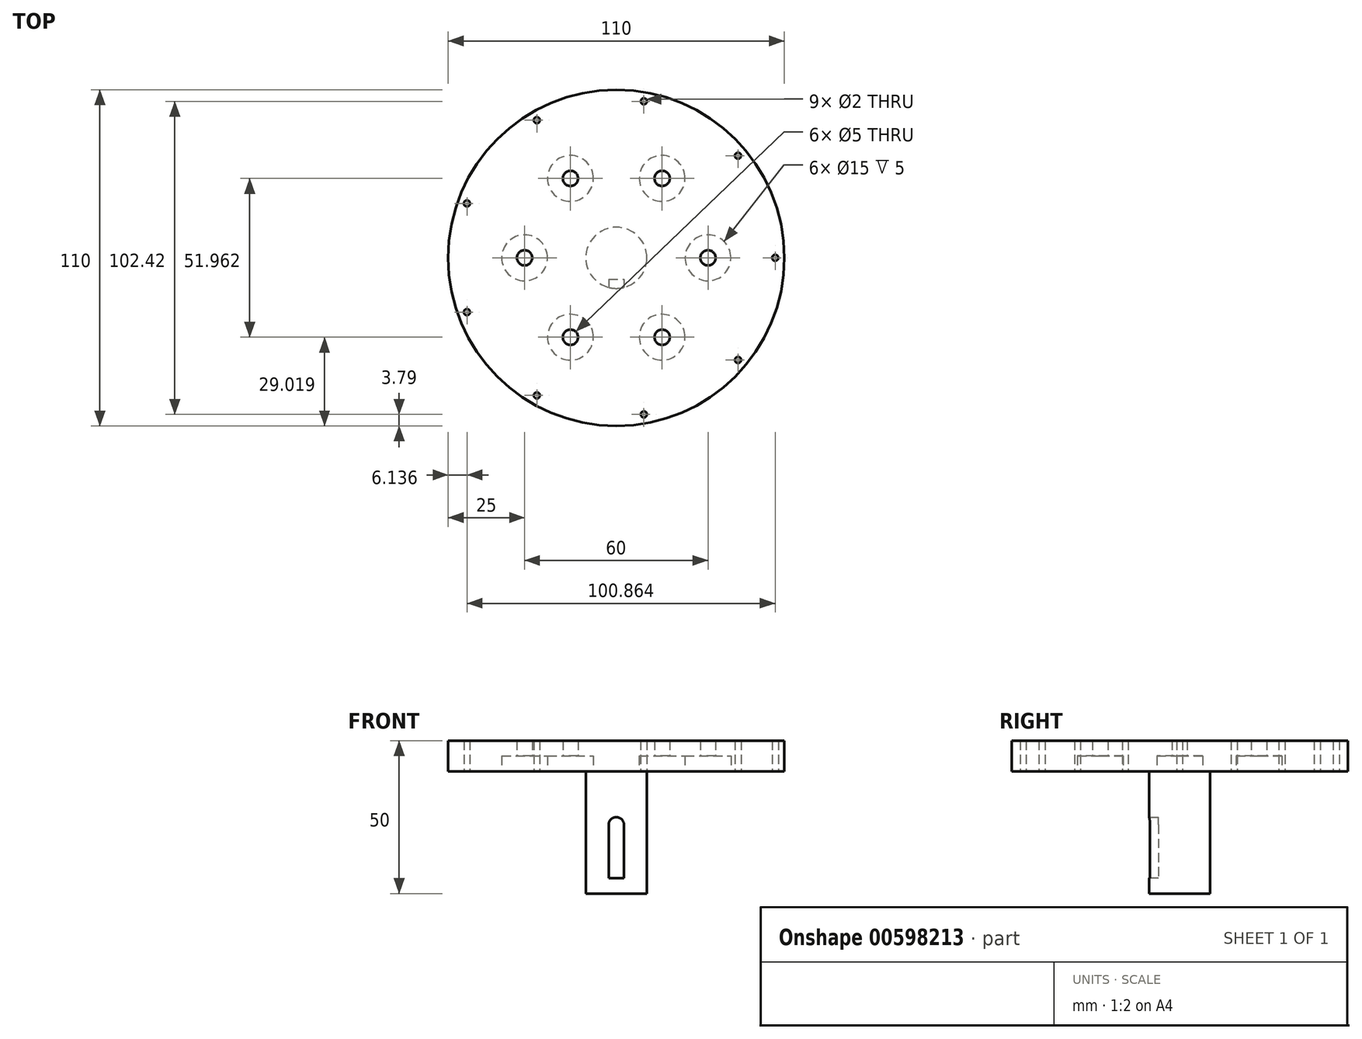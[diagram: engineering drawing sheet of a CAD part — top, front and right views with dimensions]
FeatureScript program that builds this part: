
annotation { "Feature Type Name" : "Feature", "Feature Type Description" : "" }
export const myFeature = defineFeature(function(context is Context, id is Id, definition is map)
    precondition{}
    {
        {
            var Q0;
            Q0=qCreatedBy(makeId("Top.planeOp"),FACE);
            var sketch = newSketch(context, id + "F0", { "sketchPlane" : qUnion([Q0])});
            skCircle(sketch, "E0", {"center": v(0, 0) * mm, "radius": 55 * mm});
            skCircle(sketch, "E1", {"center": v(30, 0) * mm, "radius": 2.5 * mm});
            skCircle(sketch, "E2.1.0", {"center": v(15, 25.98) * mm, "radius": 2.5 * mm});
            skCircle(sketch, "E2.2.0", {"center": v(-15, 25.98) * mm, "radius": 2.5 * mm});
            skCircle(sketch, "E2.3.0", {"center": v(-30, 0) * mm, "radius": 2.5 * mm});
            skCircle(sketch, "E2.4.0", {"center": v(-15, -25.98) * mm, "radius": 2.5 * mm});
            skCircle(sketch, "E2.5.0", {"center": v(15, -25.98) * mm, "radius": 2.5 * mm});
            skCircle(sketch, "E3", {"center": v(0, 0) * mm, "radius": 10 * mm});
            skCircle(sketch, "E4", {"center": v(52, 0) * mm, "radius": 1 * mm});
            skCircle(sketch, "E5.1.0", {"center": v(39.83, 33.42) * mm, "radius": 1 * mm});
            skCircle(sketch, "E5.2.0", {"center": v(9.03, 51.21) * mm, "radius": 1 * mm});
            skCircle(sketch, "E5.3.0", {"center": v(-26, 45.03) * mm, "radius": 1 * mm});
            skCircle(sketch, "E5.4.0", {"center": v(-48.86, 17.79) * mm, "radius": 1 * mm});
            skCircle(sketch, "E5.5.0", {"center": v(-48.86, -17.79) * mm, "radius": 1 * mm});
            skCircle(sketch, "E5.6.0", {"center": v(-26, -45.03) * mm, "radius": 1 * mm});
            skCircle(sketch, "E5.7.0", {"center": v(9.03, -51.21) * mm, "radius": 1 * mm});
            skCircle(sketch, "E5.8.0", {"center": v(39.83, -33.42) * mm, "radius": 1 * mm});
            skSolve(sketch);
        }
        {
            var Q0;
            Q0 = qSketchRegion(id + "F0", true);
            var Q1;
            Q1=makeQuery(id+"F0.imprint","IMPRINT",FACE,{"disambiguationData":[TD([[makeQuery(id+"F0.imprint","IMPRINT",EDGE,{"derivedFrom":sQuery(id+"F0.wireOp",EDGE,"E3")}),1.0]])]});
            extrude(context, id + "F1", {"entities" : qUnion([Q0, Q1]), "depth" : 50 * mm, "offsetDistance" : 25 * mm});
        }
        {
            var Q0;
            Q0 = qSketchRegion(id + "F0", true);
            var Q1;
            Q1=makeQuery(id+"F1.opExtrude","CAP_FACE",FACE,{"disambiguationData":[OSD([sQuery(id+"F0.wireOp",EDGE,"E0"),sQuery(id+"F0.wireOp",EDGE,"E1"),sQuery(id+"F0.wireOp",EDGE,"E2.1.0"),sQuery(id+"F0.wireOp",EDGE,"E2.2.0"),sQuery(id+"F0.wireOp",EDGE,"E2.3.0"),sQuery(id+"F0.wireOp",EDGE,"E2.4.0"),sQuery(id+"F0.wireOp",EDGE,"E2.5.0"),sQuery(id+"F0.wireOp",EDGE,"4EDKuiju-nCJj-Tv50-iLBq-kj0HRudPTFIA"),sQuery(id+"F0.wireOp",EDGE,"37c3f761-c143-4761-86c4-4c0452dd75e1.1.0"),sQuery(id+"F0.wireOp",EDGE,"37c3f761-c143-4761-86c4-4c0452dd75e1.2.0"),sQuery(id+"F0.wireOp",EDGE,"37c3f761-c143-4761-86c4-4c0452dd75e1.3.0"),sQuery(id+"F0.wireOp",EDGE,"37c3f761-c143-4761-86c4-4c0452dd75e1.4.0"),sQuery(id+"F0.wireOp",EDGE,"37c3f761-c143-4761-86c4-4c0452dd75e1.5.0"),sQuery(id+"F0.wireOp",EDGE,"37c3f761-c143-4761-86c4-4c0452dd75e1.6.0")])],"isStart":false});
            extrude(context, id + "F2", {"entities" : qUnion([Q0, Q1]), "operationType" : NewBodyOperationType.REMOVE, "depth" : 40 * mm, "offsetDistance" : 25 * mm});
        }
        {
            var Q0;
            Q0=makeQuery(id+"F2.boolean.opBoolean","COPY",FACE,{"derivedFrom":makeQuery(id+"F2.opExtrude","CAP_FACE",FACE,{"disambiguationData":[OSD([sQuery(id+"F0.wireOp",EDGE,"E0"),sQuery(id+"F0.wireOp",EDGE,"E1"),sQuery(id+"F0.wireOp",EDGE,"E2.1.0"),sQuery(id+"F0.wireOp",EDGE,"E2.2.0"),sQuery(id+"F0.wireOp",EDGE,"E2.3.0"),sQuery(id+"F0.wireOp",EDGE,"E2.4.0"),sQuery(id+"F0.wireOp",EDGE,"E2.5.0"),sQuery(id+"F0.wireOp",EDGE,"E3"),sQuery(id+"F0.wireOp",EDGE,"4EDKuiju-nCJj-Tv50-iLBq-kj0HRudPTFIA"),sQuery(id+"F0.wireOp",EDGE,"37c3f761-c143-4761-86c4-4c0452dd75e1.1.0"),sQuery(id+"F0.wireOp",EDGE,"37c3f761-c143-4761-86c4-4c0452dd75e1.2.0"),sQuery(id+"F0.wireOp",EDGE,"37c3f761-c143-4761-86c4-4c0452dd75e1.3.0"),sQuery(id+"F0.wireOp",EDGE,"37c3f761-c143-4761-86c4-4c0452dd75e1.4.0"),sQuery(id+"F0.wireOp",EDGE,"37c3f761-c143-4761-86c4-4c0452dd75e1.5.0"),sQuery(id+"F0.wireOp",EDGE,"37c3f761-c143-4761-86c4-4c0452dd75e1.6.0")])],"isStart":false})});
            var sketch = newSketch(context, id + "F3", { "sketchPlane" : qUnion([Q0])});
            skCircle(sketch, "E6", {"center": v(15, -25.98) * mm, "radius": 7.5 * mm});
            skCircle(sketch, "E7.1.0", {"center": v(30, 0) * mm, "radius": 7.5 * mm});
            skCircle(sketch, "E7.2.0", {"center": v(15, 25.98) * mm, "radius": 7.5 * mm});
            skCircle(sketch, "E7.3.0", {"center": v(-15, 25.98) * mm, "radius": 7.5 * mm});
            skCircle(sketch, "E7.4.0", {"center": v(-30, 0) * mm, "radius": 7.5 * mm});
            skCircle(sketch, "E7.5.0", {"center": v(-15, -25.98) * mm, "radius": 7.5 * mm});
            skPoint(sketch, "E7.center", {"position": v(0, 0) * mm});
            skSolve(sketch);
        }
        {
            var Q0;
            Q0=makeQuery(id+"F3.imprint","IMPRINT",FACE,{"disambiguationData":[TD([[makeQuery(id+"F3.imprint","IMPRINT",EDGE,{"derivedFrom":sQuery(id+"F3.wireOp",EDGE,"E6")}),1.0]])]});
            var Q1;
            Q1=makeQuery(id+"F3.imprint","IMPRINT",FACE,{"disambiguationData":[TD([[makeQuery(id+"F3.imprint","IMPRINT",EDGE,{"derivedFrom":sQuery(id+"F3.wireOp",EDGE,"E7.1.0")}),1.0]])]});
            var Q2;
            Q2=makeQuery(id+"F3.imprint","IMPRINT",FACE,{"disambiguationData":[TD([[makeQuery(id+"F3.imprint","IMPRINT",EDGE,{"derivedFrom":sQuery(id+"F3.wireOp",EDGE,"E7.5.0")}),1.0]])]});
            var Q3;
            Q3=makeQuery(id+"F3.imprint","IMPRINT",FACE,{"disambiguationData":[TD([[makeQuery(id+"F3.imprint","IMPRINT",EDGE,{"derivedFrom":sQuery(id+"F3.wireOp",EDGE,"E7.2.0")}),1.0]])]});
            var Q4;
            Q4=makeQuery(id+"F3.imprint","IMPRINT",FACE,{"disambiguationData":[TD([[makeQuery(id+"F3.imprint","IMPRINT",EDGE,{"derivedFrom":sQuery(id+"F3.wireOp",EDGE,"E7.3.0")}),1.0]])]});
            var Q5;
            Q5=makeQuery(id+"F3.imprint","IMPRINT",FACE,{"disambiguationData":[TD([[makeQuery(id+"F3.imprint","IMPRINT",EDGE,{"derivedFrom":sQuery(id+"F3.wireOp",EDGE,"E7.4.0")}),1.0]])]});
            extrude(context, id + "F4", {"entities" : qUnion([Q0, Q1, Q2, Q3, Q4, Q5]), "operationType" : NewBodyOperationType.REMOVE, "oppositeDirection" : true, "depth" : 5 * mm, "offsetDistance" : 25 * mm});
        }
        {
            var Q0;
            Q0=makeQuery(id+"F1.opExtrude","CAP_FACE",FACE,{"disambiguationData":[OSD([sQuery(id+"F0.wireOp",EDGE,"E0"),sQuery(id+"F0.wireOp",EDGE,"E1"),sQuery(id+"F0.wireOp",EDGE,"E2.1.0"),sQuery(id+"F0.wireOp",EDGE,"E2.2.0"),sQuery(id+"F0.wireOp",EDGE,"E2.3.0"),sQuery(id+"F0.wireOp",EDGE,"E2.4.0"),sQuery(id+"F0.wireOp",EDGE,"E2.5.0"),sQuery(id+"F0.wireOp",EDGE,"4EDKuiju-nCJj-Tv50-iLBq-kj0HRudPTFIA"),sQuery(id+"F0.wireOp",EDGE,"37c3f761-c143-4761-86c4-4c0452dd75e1.1.0"),sQuery(id+"F0.wireOp",EDGE,"37c3f761-c143-4761-86c4-4c0452dd75e1.2.0"),sQuery(id+"F0.wireOp",EDGE,"37c3f761-c143-4761-86c4-4c0452dd75e1.3.0"),sQuery(id+"F0.wireOp",EDGE,"37c3f761-c143-4761-86c4-4c0452dd75e1.4.0"),sQuery(id+"F0.wireOp",EDGE,"37c3f761-c143-4761-86c4-4c0452dd75e1.5.0"),sQuery(id+"F0.wireOp",EDGE,"37c3f761-c143-4761-86c4-4c0452dd75e1.6.0")])],"isStart":true});
            var sketch = newSketch(context, id + "F5", { "sketchPlane" : qUnion([Q0])});
            skLineSegment(sketch, "E8", {"start": v(0, 0) * mm, "end": v(0, 7) * mm});
            skLineSegment(sketch, "E9", {"start": v(0, 7) * mm, "end": v(2.5, 7) * mm});
            skLineSegment(sketch, "E10", {"start": v(2.5, 7) * mm, "end": v(2.5, 14.92) * mm});
            skLineSegment(sketch, "E11.MirrorCS", {"start": v(-2.5, 7) * mm, "end": v(-2.5, 14.92) * mm});
            skLineSegment(sketch, "E12.MirrorCS", {"start": v(0, 7) * mm, "end": v(-2.5, 7) * mm});
            skSolve(sketch);
        }
        {
            var Q0;
            {var subQ5=sQuery(id+"F5.wireOp",EDGE,"E9");Q0=makeQuery(id+"F5.imprint","IMPRINT",FACE,{"disambiguationData":[TD([[makeQuery(id+"F5.imprint","IMPRINT",EDGE,{"derivedFrom":subQ5}),1.0]])]});}
            extrude(context, id + "F6", {"entities" : qUnion([Q0]), "operationType" : NewBodyOperationType.REMOVE, "oppositeDirection" : true, "depth" : 25 * mm, "offsetDistance" : 25 * mm});
        }
        {
            var Q0;
            {var subQ5=sQuery(id+"F5.wireOp",EDGE,"E9");Q0=makeQuery(id+"F5.imprint","IMPRINT",FACE,{"disambiguationData":[TD([[makeQuery(id+"F5.imprint","IMPRINT",EDGE,{"derivedFrom":subQ5}),1.0]])]});}
            extrude(context, id + "F7", {"entities" : qUnion([Q0]), "operationType" : NewBodyOperationType.ADD, "depth" : -5 * mm, "offsetDistance" : 25 * mm});
        }
        {
            var Q0;
            Q0=makeQuery(id+"F6.boolean.opBoolean","COPY",EDGE,{"derivedFrom":makeQuery(id+"F6.opExtrude","CAP_EDGE",EDGE,{"disambiguationData":[OSD([sQuery(id+"F5.wireOp",EDGE,"E11.MirrorCS")])],"isStart":false})});
            var Q1;
            Q1=makeQuery(id+"F6.boolean.opBoolean","COPY",EDGE,{"derivedFrom":makeQuery(id+"F6.opExtrude","CAP_EDGE",EDGE,{"disambiguationData":[OSD([sQuery(id+"F5.wireOp",EDGE,"E10")])],"isStart":false})});
            var Q2;
            Q2=makeQuery(id+"F7.opExtrude","CAP_EDGE",EDGE,{"disambiguationData":[OSD([sQuery(id+"F5.wireOp",EDGE,"E10")])],"isStart":false});
            var Q3;
            Q3=makeQuery(id+"F7.opExtrude","CAP_EDGE",EDGE,{"disambiguationData":[OSD([sQuery(id+"F5.wireOp",EDGE,"E11.MirrorCS")])],"isStart":false});
            fillet(context, id + "F8", {"entities" : qUnion([Q0, Q1, Q2, Q3]), "radius" : 2.5 * mm, "tangentPropagation" : true, "allowEdgeOverflow" : false});
        }
    });
